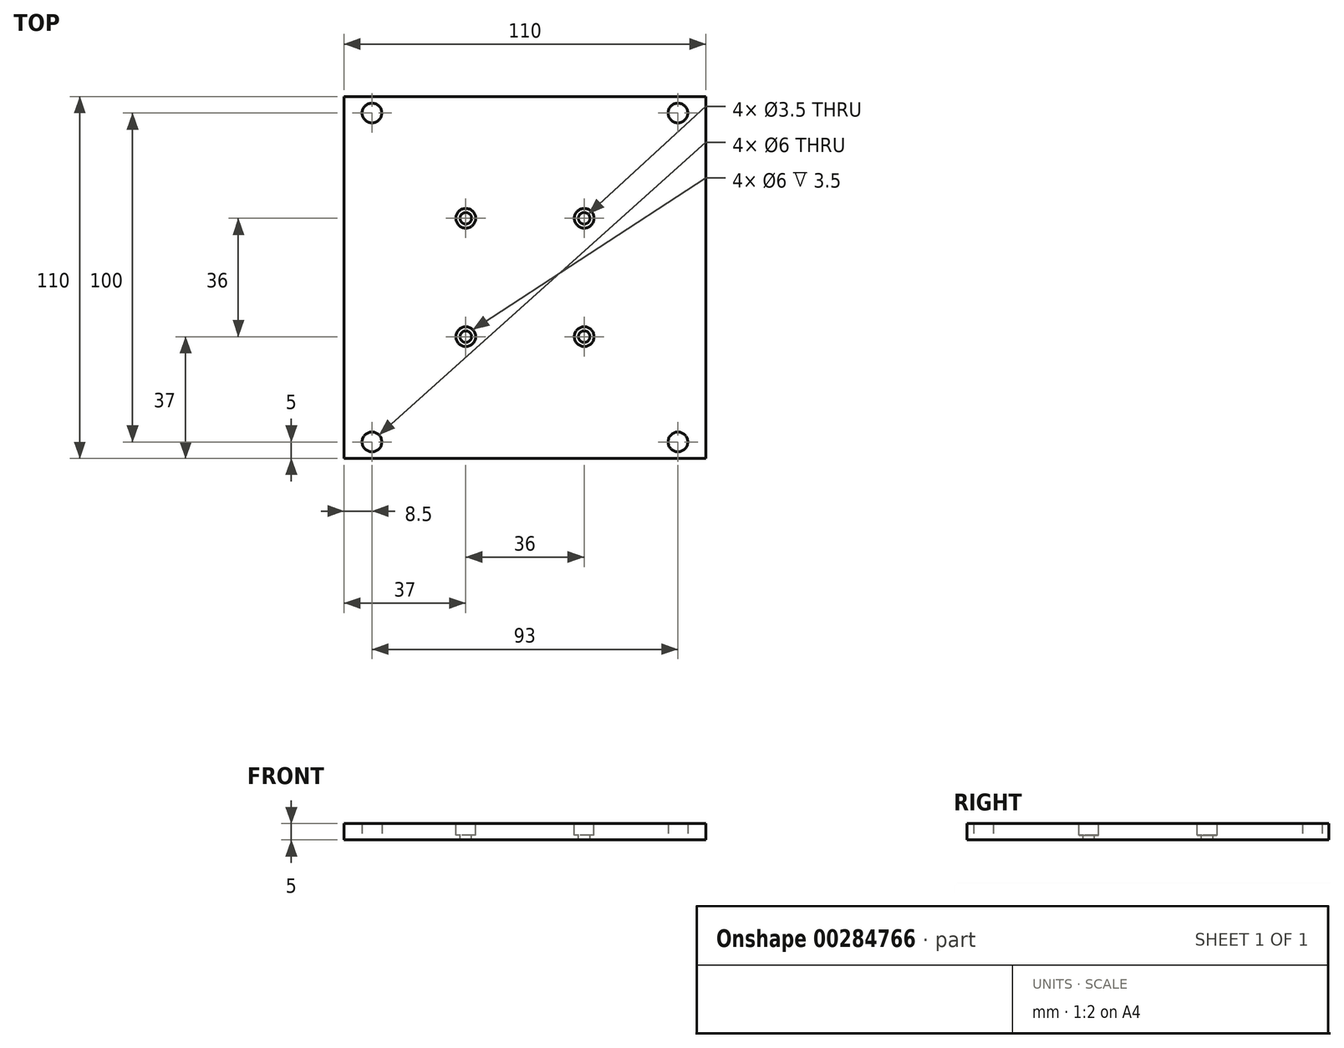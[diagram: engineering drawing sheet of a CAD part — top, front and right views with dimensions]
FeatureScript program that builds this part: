
annotation { "Feature Type Name" : "Feature", "Feature Type Description" : "" }
export const myFeature = defineFeature(function(context is Context, id is Id, definition is map)
    precondition{}
    {
        {
            var Q0;
            Q0=qCreatedBy(makeId("Top.planeOp"),FACE);
            var sketch = newSketch(context, id + "F0", { "sketchPlane" : qUnion([Q0])});
            skLineSegment(sketch, "E0.bottom", {"start": v(-55, 55) * mm, "end": v(55, 55) * mm});
            skLineSegment(sketch, "E0.top", {"start": v(-55, -55) * mm, "end": v(55, -55) * mm});
            skLineSegment(sketch, "E0.left", {"start": v(-55, 55) * mm, "end": v(-55, -55) * mm});
            skLineSegment(sketch, "E0.right", {"start": v(55, 55) * mm, "end": v(55, -55) * mm});
            skCircle(sketch, "E1", {"center": v(-46.5, 50) * mm, "radius": 3 * mm});
            skCircle(sketch, "E2", {"center": v(46.5, 50) * mm, "radius": 3 * mm});
            skCircle(sketch, "E3", {"center": v(46.5, -50) * mm, "radius": 3 * mm});
            skCircle(sketch, "E4", {"center": v(-46.5, -50) * mm, "radius": 3 * mm});
            skSolve(sketch);
        }
        {
            var Q0;
            Q0 = qSketchRegion(id + "F0", true);
            extrude(context, id + "F1", {"entities" : qUnion([Q0]), "depth" : 5 * mm});
        }
        {
            var Q0;
            Q0=makeQuery(id+"F1.opExtrude","CAP_FACE",FACE,{"disambiguationData":[OSD([sQuery(id+"F0.wireOp",EDGE,"E0.bottom"),sQuery(id+"F0.wireOp",EDGE,"E0.top"),sQuery(id+"F0.wireOp",EDGE,"E0.left"),sQuery(id+"F0.wireOp",EDGE,"E0.right"),sQuery(id+"F0.wireOp",EDGE,"E1"),sQuery(id+"F0.wireOp",EDGE,"E2"),sQuery(id+"F0.wireOp",EDGE,"E3"),sQuery(id+"F0.wireOp",EDGE,"E4")])],"isStart":false});
            var sketch = newSketch(context, id + "F2", { "sketchPlane" : qUnion([Q0])});
            skCircle(sketch, "E5", {"center": v(-18, 18) * mm, "radius": 1.75 * mm});
            skCircle(sketch, "E6", {"center": v(18, 18) * mm, "radius": 1.75 * mm});
            skCircle(sketch, "E7", {"center": v(-18, -18) * mm, "radius": 1.75 * mm});
            skCircle(sketch, "E8", {"center": v(18, -18) * mm, "radius": 1.75 * mm});
            skSolve(sketch);
        }
        {
            var Q0;
            Q0 = qSketchRegion(id + "F2", true);
            extrude(context, id + "F3", {"entities" : qUnion([Q0]), "operationType" : NewBodyOperationType.REMOVE, "endBound" : BoundingType.THROUGH_ALL, "oppositeDirection" : true, "depth" : 25 * mm});
        }
        {
            var Q0;
            Q0=makeQuery(id+"F1.opExtrude","CAP_FACE",FACE,{"disambiguationData":[OSD([sQuery(id+"F0.wireOp",EDGE,"E0.bottom"),sQuery(id+"F0.wireOp",EDGE,"E0.top"),sQuery(id+"F0.wireOp",EDGE,"E0.left"),sQuery(id+"F0.wireOp",EDGE,"E0.right"),sQuery(id+"F0.wireOp",EDGE,"E1"),sQuery(id+"F0.wireOp",EDGE,"E2"),sQuery(id+"F0.wireOp",EDGE,"E3"),sQuery(id+"F0.wireOp",EDGE,"E4")])],"isStart":false});
            var sketch = newSketch(context, id + "F4", { "sketchPlane" : qUnion([Q0])});
            skCircle(sketch, "E9", {"center": v(-18, 18) * mm, "radius": 3 * mm});
            skCircle(sketch, "E10", {"center": v(-18, -18) * mm, "radius": 3 * mm});
            skCircle(sketch, "E11", {"center": v(18, 18) * mm, "radius": 3 * mm});
            skCircle(sketch, "E12", {"center": v(18, -18) * mm, "radius": 3 * mm});
            skSolve(sketch);
        }
        {
            var Q0;
            Q0 = qSketchRegion(id + "F4", true);
            extrude(context, id + "F5", {"entities" : qUnion([Q0]), "operationType" : NewBodyOperationType.REMOVE, "oppositeDirection" : true, "depth" : 3.5 * mm});
        }
    });
